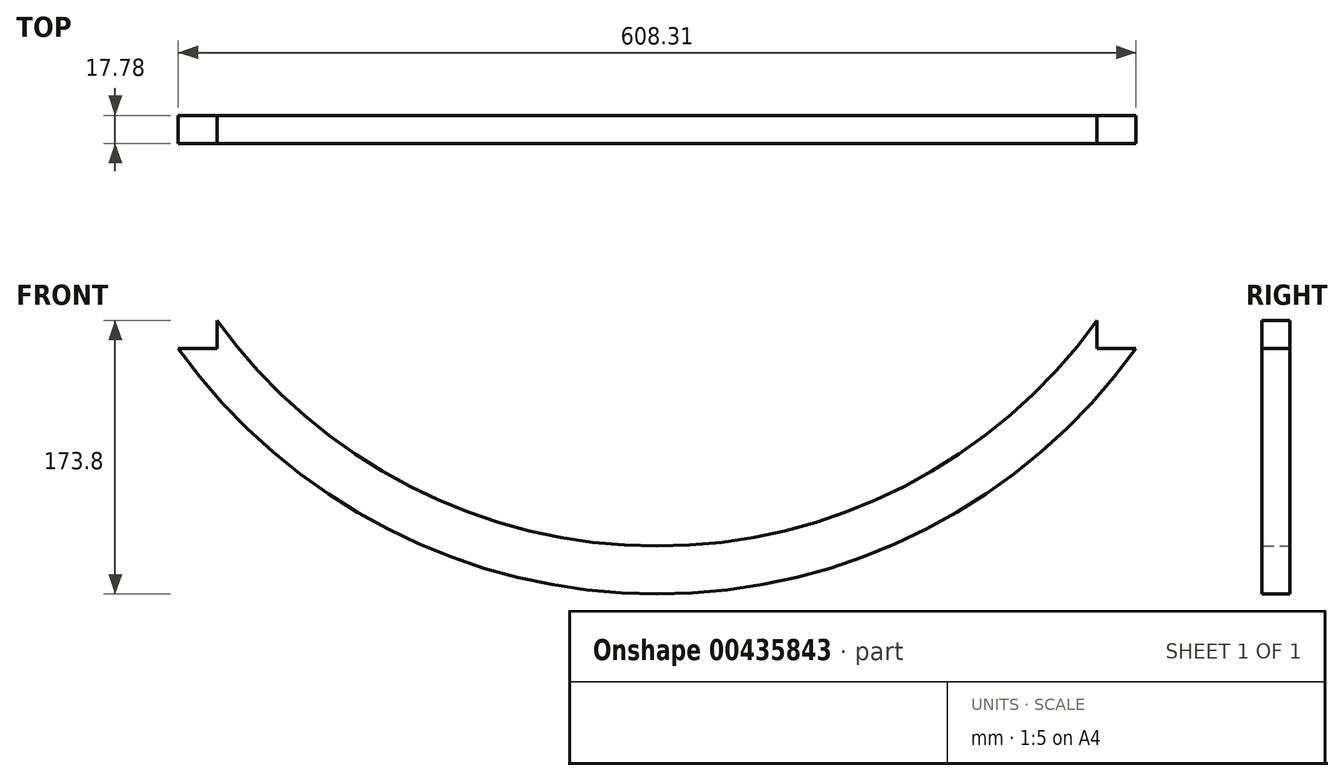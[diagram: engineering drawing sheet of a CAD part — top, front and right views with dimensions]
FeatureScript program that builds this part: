
annotation { "Feature Type Name" : "Feature", "Feature Type Description" : "" }
export const myFeature = defineFeature(function(context is Context, id is Id, definition is map)
    precondition{}
    {
        {
            var Q0;
            Q0=qCreatedBy(makeId("Front.planeOp"),FACE);
            var sketch = newSketch(context, id + "F0", { "sketchPlane" : qUnion([Q0])});
            skArc(sketch, "E0", {"start": v(134.4, 3.81) * mm, "mid": v(291.4, 41.73) * mm, "end": v(413.8, 147.13) * mm});
            skArc(sketch, "E1.0", {"start": v(134.4, -26.67) * mm, "mid": v(305.31, 14.61) * mm, "end": v(438.55, 129.35) * mm});
            skLineSegment(sketch, "E2", {"start": v(134.4, 3.81) * mm, "end": v(134.4, -26.67) * mm});
            skLineSegment(sketch, "E3", {"start": v(413.8, 147.13) * mm, "end": v(413.8, 129.35) * mm});
            skLineSegment(sketch, "E4", {"start": v(438.55, 129.35) * mm, "end": v(413.8, 129.35) * mm});
            skSolve(sketch);
        }
        {
            var Q0;
            Q0 = qSketchRegion(id + "F0", true);
            extrude(context, id + "F1", {"entities" : qUnion([Q0]), "depth" : 17.78 * mm});
        }
        {
            var Q0;
            Q0=makeQuery(id+"F1.opExtrude","SWEPT_BODY",BODY,{"disambiguationData":[OSD([sQuery(id+"F0.wireOp",EDGE,"E0"),sQuery(id+"F0.wireOp",EDGE,"E1.0"),sQuery(id+"F0.wireOp",EDGE,"E2"),sQuery(id+"F0.wireOp",EDGE,"E3"),sQuery(id+"F0.wireOp",EDGE,"E4")])]});
            var Q1;
            Q1=makeQuery(id+"F1.opExtrude","SWEPT_FACE",FACE,{"disambiguationData":[OSD([sQuery(id+"F0.wireOp",EDGE,"E2")])]});
            mirror(context, id + "F2", {"operationType" : NewBodyOperationType.ADD, "entities" : qUnion([Q0]), "mirrorPlane" : qUnion([Q1])});
        }
    });
